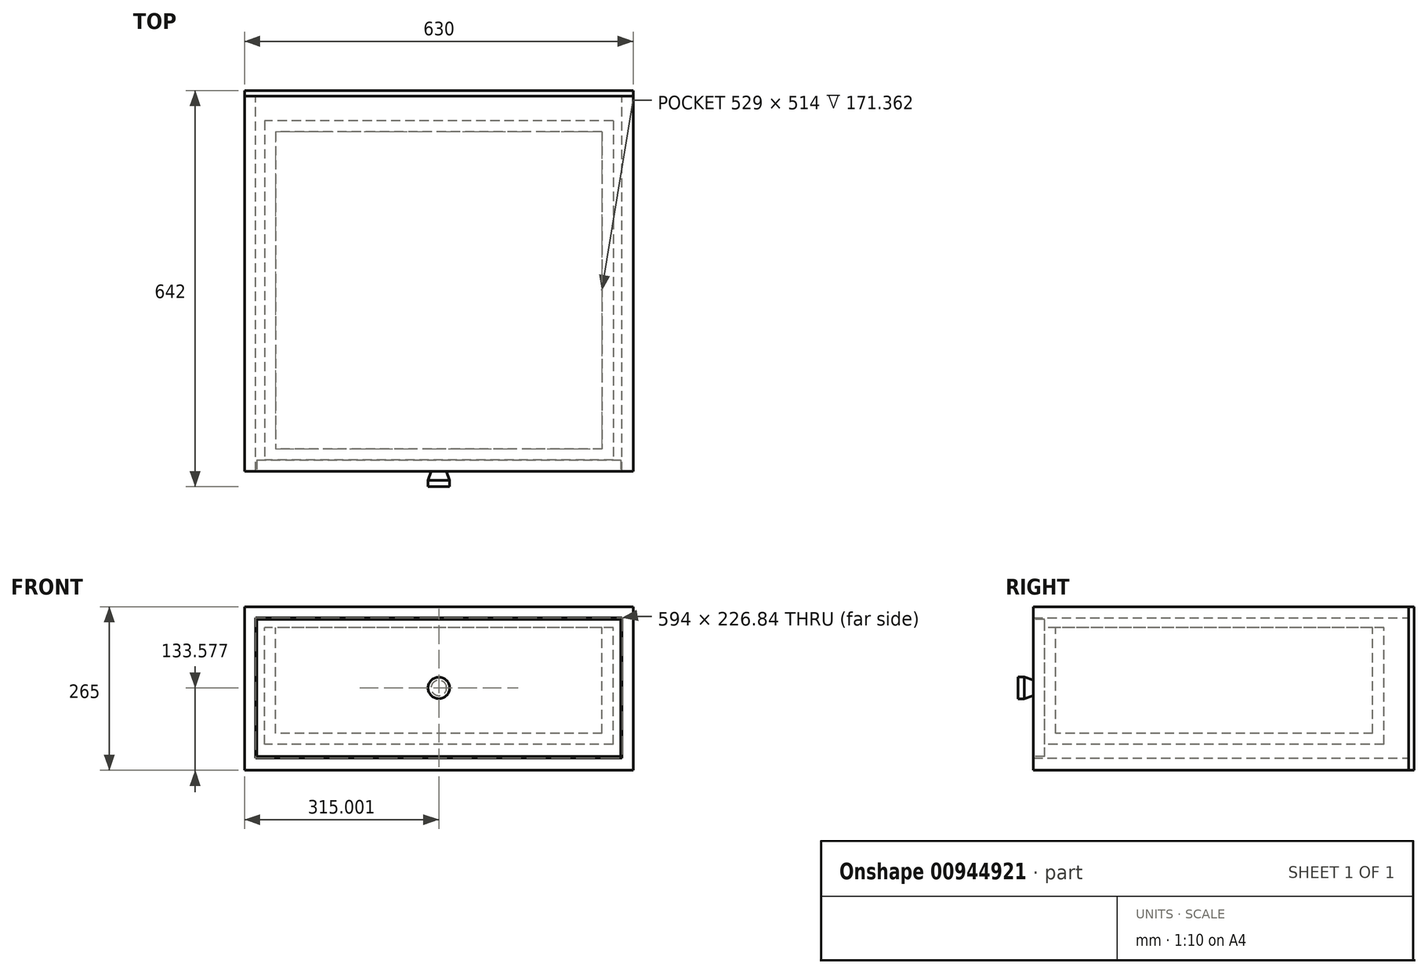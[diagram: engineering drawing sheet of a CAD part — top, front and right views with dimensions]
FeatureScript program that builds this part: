
annotation { "Feature Type Name" : "Feature", "Feature Type Description" : "" }
export const myFeature = defineFeature(function(context is Context, id is Id, definition is map)
    precondition{}
    {
        {
            var Q0;
            Q0=qCreatedBy(makeId("Front.planeOp"),FACE);
            var sketch = newSketch(context, id + "F0", { "sketchPlane" : qUnion([Q0])});
            skLineSegment(sketch, "E0", {"start": v(-326.85, -71.54) * mm, "end": v(-326.85, 193.46) * mm});
            skLineSegment(sketch, "E1.1", {"start": v(-308.85, -51.38) * mm, "end": v(-308.85, 175.46) * mm});
            skLineSegment(sketch, "E2.trimOffspring", {"start": v(285.15, -51.38) * mm, "end": v(-308.85, -51.38) * mm});
            skLineSegment(sketch, "E3.top", {"start": v(-308.85, 175.46) * mm, "end": v(285.15, 175.46) * mm});
            skLineSegment(sketch, "E4.trimOffspring", {"start": v(285.15, 175.46) * mm, "end": v(285.15, -51.38) * mm});
            skLineSegment(sketch, "E5", {"start": v(-326.85, 193.46) * mm, "end": v(303.15, 193.46) * mm});
            skLineSegment(sketch, "E6", {"start": v(303.15, -71.54) * mm, "end": v(303.15, 193.46) * mm});
            skLineSegment(sketch, "E7", {"start": v(-326.85, -71.54) * mm, "end": v(303.15, -71.54) * mm});
            skLineSegment(sketch, "E8", {"start": v(-326.85, -71.54) * mm, "end": v(-326.85, 463.46) * mm, "construction": true});
            skLineSegment(sketch, "E9", {"start": v(-326.85, 463.46) * mm, "end": v(933.15, 1328.46) * mm, "construction": true});
            skLineSegment(sketch, "E10", {"start": v(933.15, 1328.46) * mm, "end": v(933.15, -71.54) * mm, "construction": true});
            skLineSegment(sketch, "E11.bottom", {"start": v(-326.85, 193.46) * mm, "end": v(303.15, 193.46) * mm, "construction": true});
            skLineSegment(sketch, "E11.top", {"start": v(-326.85, 458.46) * mm, "end": v(303.15, 458.46) * mm, "construction": true});
            skLineSegment(sketch, "E11.left", {"start": v(-326.85, 193.46) * mm, "end": v(-326.85, 458.46) * mm, "construction": true});
            skLineSegment(sketch, "E11.right", {"start": v(303.15, 193.46) * mm, "end": v(303.15, 458.46) * mm, "construction": true});
            skLineSegment(sketch, "E12.bottom", {"start": v(303.15, 193.46) * mm, "end": v(933.15, 193.46) * mm, "construction": true});
            skLineSegment(sketch, "E12.top", {"start": v(303.15, -71.54) * mm, "end": v(933.15, -71.54) * mm, "construction": true});
            skLineSegment(sketch, "E12.left", {"start": v(303.15, 193.46) * mm, "end": v(303.15, -71.54) * mm, "construction": true});
            skLineSegment(sketch, "E12.right", {"start": v(933.15, 193.46) * mm, "end": v(933.15, -71.54) * mm, "construction": true});
            skLineSegment(sketch, "E13.bottom", {"start": v(303.15, 458.46) * mm, "end": v(933.15, 458.46) * mm, "construction": true});
            skLineSegment(sketch, "E13.left", {"start": v(303.15, 458.46) * mm, "end": v(303.15, 193.46) * mm, "construction": true});
            skLineSegment(sketch, "E13.right", {"start": v(933.15, 458.46) * mm, "end": v(933.15, 193.46) * mm, "construction": true});
            skLineSegment(sketch, "E14.bottom", {"start": v(933.15, 458.46) * mm, "end": v(113.15, 458.46) * mm, "construction": true});
            skLineSegment(sketch, "E14.top", {"start": v(933.15, 758.46) * mm, "end": v(113.15, 758.46) * mm, "construction": true});
            skLineSegment(sketch, "E14.left", {"start": v(933.15, 458.46) * mm, "end": v(933.15, 758.46) * mm, "construction": true});
            skLineSegment(sketch, "E14.right", {"start": v(113.15, 458.46) * mm, "end": v(113.15, 758.46) * mm, "construction": true});
            skLineSegment(sketch, "E15.bottom", {"start": v(933.15, 758.46) * mm, "end": v(523.15, 758.46) * mm, "construction": true});
            skLineSegment(sketch, "E15.top", {"start": v(933.15, 1043.46) * mm, "end": v(523.15, 1043.46) * mm, "construction": true});
            skLineSegment(sketch, "E15.left", {"start": v(933.15, 758.46) * mm, "end": v(933.15, 1043.46) * mm, "construction": true});
            skLineSegment(sketch, "E15.right", {"start": v(523.15, 758.46) * mm, "end": v(523.15, 1043.46) * mm, "construction": true});
            skSolve(sketch);
        }
        {
            var Q0;
            Q0=qSketchRegion(id+"F0",true);
            extrude(context, id + "F1", {"entities" : qUnion([Q0]), "depth" : 608 * mm, "offsetDistance" : 25 * mm});
        }
        {
            var Q0;
            Q0=makeQuery(id+"F1.opExtrude","CAP_FACE",FACE,{"disambiguationData":[OSD([sQuery(id+"F0.wireOp",EDGE,"E0"),sQuery(id+"F0.wireOp",EDGE,"1bbb11d5-5f90-4ef2-9ceb-a32cb31813a0"),sQuery(id+"F0.wireOp",EDGE,"E1.1"),sQuery(id+"F0.wireOp",EDGE,"E2.trimOffspring"),sQuery(id+"F0.wireOp",EDGE,"E3.top"),sQuery(id+"F0.wireOp",EDGE,"E4.trimOffspring"),sQuery(id+"F0.wireOp",EDGE,"E5"),sQuery(id+"F0.wireOp",EDGE,"E6")])],"isStart":true});
            var sketch = newSketch(context, id + "F2", { "sketchPlane" : qUnion([Q0])});
            skLineSegment(sketch, "E16.left", {"start": v(-303.15, 193.46) * mm, "end": v(-303.15, 193.46) * mm});
            skLineSegment(sketch, "E16.right", {"start": v(326.85, 193.46) * mm, "end": v(326.85, 193.46) * mm});
            skLineSegment(sketch, "E17.bottom", {"start": v(-303.15, 193.46) * mm, "end": v(326.85, 193.46) * mm});
            skLineSegment(sketch, "E17.top", {"start": v(-303.15, -71.54) * mm, "end": v(326.85, -71.54) * mm});
            skLineSegment(sketch, "E17.left", {"start": v(-303.15, 193.46) * mm, "end": v(-303.15, -71.54) * mm});
            skLineSegment(sketch, "E17.right", {"start": v(326.85, 193.46) * mm, "end": v(326.85, -71.54) * mm});
            skSolve(sketch);
        }
        {
            var Q0;
            Q0=qSketchRegion(id+"F2",true);
            extrude(context, id + "F3", {"entities" : qUnion([Q0]), "depth" : 9 * mm, "offsetDistance" : 25 * mm});
        }
        {
            var Q0;
            Q0=makeQuery(id+"F1.opExtrude","CAP_FACE",FACE,{"disambiguationData":[OSD([sQuery(id+"F0.wireOp",EDGE,"E0"),sQuery(id+"F0.wireOp",EDGE,"1bbb11d5-5f90-4ef2-9ceb-a32cb31813a0"),sQuery(id+"F0.wireOp",EDGE,"E1.1"),sQuery(id+"F0.wireOp",EDGE,"E2.trimOffspring"),sQuery(id+"F0.wireOp",EDGE,"E3.top"),sQuery(id+"F0.wireOp",EDGE,"E4.trimOffspring"),sQuery(id+"F0.wireOp",EDGE,"E5"),sQuery(id+"F0.wireOp",EDGE,"E6")])],"isStart":false});
            var sketch = newSketch(context, id + "F4", { "sketchPlane" : qUnion([Q0])});
            skLineSegment(sketch, "E18.0", {"start": v(-306.85, 173.46) * mm, "end": v(283.15, 173.46) * mm});
            skLineSegment(sketch, "E18.1", {"start": v(-306.85, -49.38) * mm, "end": v(-306.85, 173.46) * mm});
            skLineSegment(sketch, "E18.2", {"start": v(283.15, -49.38) * mm, "end": v(-306.85, -49.38) * mm});
            skLineSegment(sketch, "E18.3", {"start": v(283.15, 173.46) * mm, "end": v(283.15, -49.38) * mm});
            skSolve(sketch);
        }
        {
            var Q0;
            Q0=qSketchRegion(id+"F4",true);
            extrude(context, id + "F5", {"entities" : qUnion([Q0]), "oppositeDirection" : true, "depth" : 18 * mm, "offsetDistance" : 25 * mm});
        }
        {
            var Q0;
            Q0=makeQuery(id+"F5.opExtrude","CAP_FACE",FACE,{"disambiguationData":[OSD([sQuery(id+"F4.wireOp",EDGE,"E18.0"),sQuery(id+"F4.wireOp",EDGE,"E18.1"),sQuery(id+"F4.wireOp",EDGE,"E18.2"),sQuery(id+"F4.wireOp",EDGE,"E18.3")])],"isStart":false});
            var sketch = newSketch(context, id + "F6", { "sketchPlane" : qUnion([Q0])});
            skLineSegment(sketch, "E19.bottom", {"start": v(-270.65, -29.38) * mm, "end": v(294.35, -29.38) * mm});
            skLineSegment(sketch, "E19.top", {"start": v(-270.65, 159.98) * mm, "end": v(294.35, 159.98) * mm});
            skLineSegment(sketch, "E19.left", {"start": v(-270.65, -29.38) * mm, "end": v(-270.65, 159.98) * mm});
            skLineSegment(sketch, "E19.right", {"start": v(294.35, -29.38) * mm, "end": v(294.35, 159.98) * mm});
            skSolve(sketch);
        }
        {
            var Q0;
            Q0=qSketchRegion(id+"F6",true);
            extrude(context, id + "F7", {"entities" : qUnion([Q0]), "depth" : 550 * mm, "offsetDistance" : 25 * mm});
        }
        {
            var Q0;
            Q0=makeQuery(id+"F7.opExtrude","SWEPT_FACE",FACE,{"disambiguationData":[OSD([sQuery(id+"F6.wireOp",EDGE,"E19.top")])]});
            shell(context, id + "F8", {"entities" : qUnion([Q0]), "thickness" : 18 * mm});
        }
        {
            var Q0;
            Q0=makeQuery(id+"F5.opExtrude","CAP_FACE",FACE,{"disambiguationData":[OSD([sQuery(id+"F4.wireOp",EDGE,"E18.0"),sQuery(id+"F4.wireOp",EDGE,"E18.1"),sQuery(id+"F4.wireOp",EDGE,"E18.2"),sQuery(id+"F4.wireOp",EDGE,"E18.3")])],"isStart":true});
            var sketch = newSketch(context, id + "F9", { "sketchPlane" : qUnion([Q0])});
            skLineSegment(sketch, "E20", {"start": v(283.15, 62.04) * mm, "end": v(-306.85, 62.04) * mm, "construction": true});
            skCircle(sketch, "E21", {"center": v(-11.85, 62.04) * mm, "radius": 17.5 * mm});
            skSolve(sketch);
        }
        {
            var Q0;
            Q0=qSketchRegion(id+"F9",true);
            extrude(context, id + "F10", {"entities" : qUnion([Q0]), "depth" : 25 * mm, "offsetDistance" : 25 * mm});
        }
        {
            var Q0;
            Q0=makeQuery(id+"F10.opExtrude","CAP_EDGE",EDGE,{"disambiguationData":[OSD([sQuery(id+"F9.wireOp",EDGE,"E21")])],"isStart":true});
            chamfer(context, id + "F11", {"entities" : qUnion([Q0]), "chamferType" : ChamferType.TWO_OFFSETS, "width1" : 15 * mm, "oppositeDirection" : false, "width2" : 5 * mm, "tangentPropagation" : true});
        }
    });
